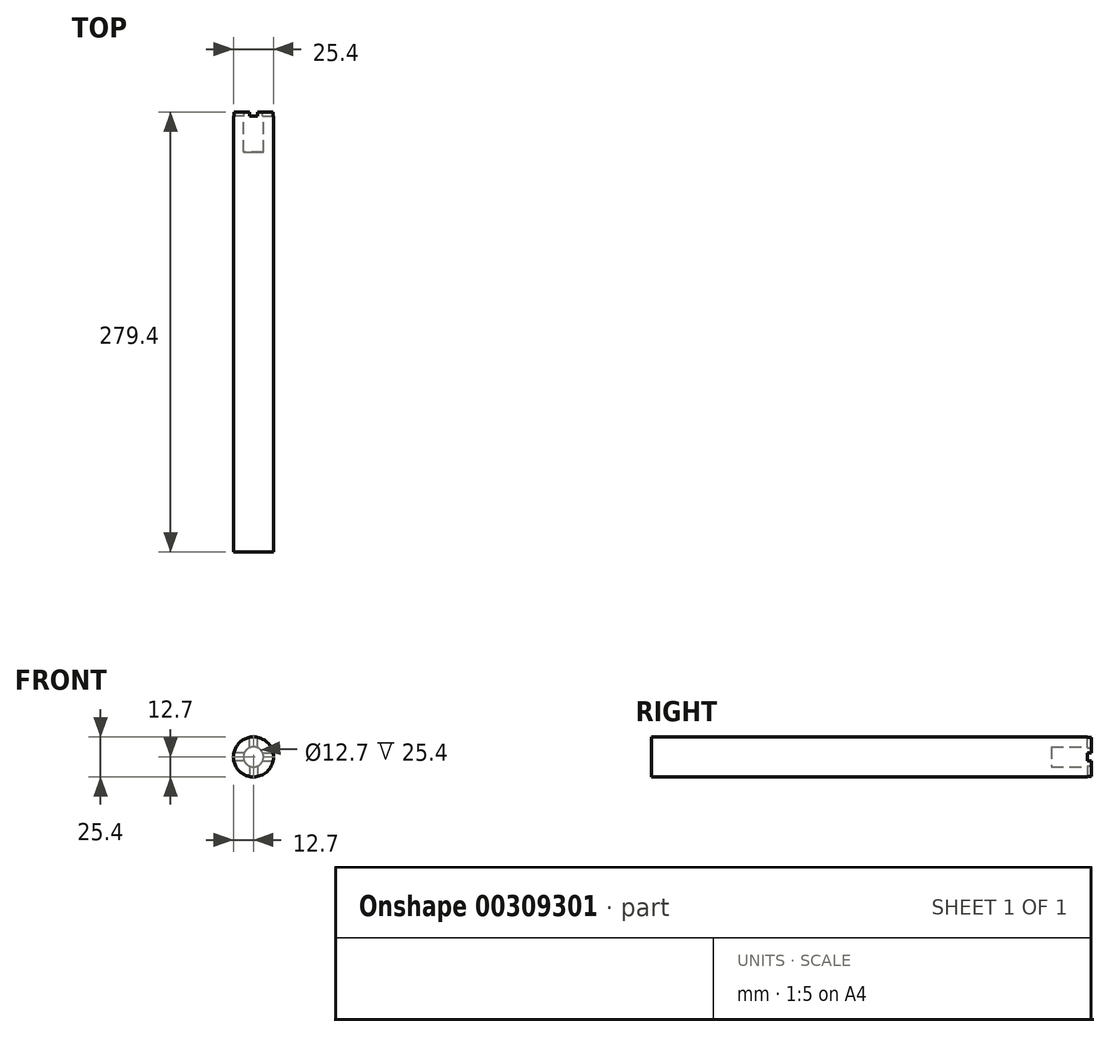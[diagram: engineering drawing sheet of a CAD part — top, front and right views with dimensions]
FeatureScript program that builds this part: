
annotation { "Feature Type Name" : "Feature", "Feature Type Description" : "" }
export const myFeature = defineFeature(function(context is Context, id is Id, definition is map)
    precondition{}
    {
        {
            var Q0;
            Q0=qCreatedBy(makeId("Front.planeOp"),FACE);
            var sketch = newSketch(context, id + "F0", { "sketchPlane" : qUnion([Q0])});
            skCircle(sketch, "E0", {"center": v(0, 0) * mm, "radius": 12.7 * mm});
            skSolve(sketch);
        }
        {
            var Q0;
            Q0 = qSketchRegion(id + "F0", true);
            extrude(context, id + "F1", {"entities" : qUnion([Q0]), "depth" : 279.4 * mm});
        }
        {
            var Q0;
            Q0=makeQuery(id+"F1.opExtrude","CAP_FACE",FACE,{"disambiguationData":[OSD([sQuery(id+"F0.wireOp",EDGE,"E0")])],"isStart":true});
            var sketch = newSketch(context, id + "F2", { "sketchPlane" : qUnion([Q0])});
            skCircle(sketch, "E1", {"center": v(0, 0) * mm, "radius": 6.35 * mm});
            skLineSegment(sketch, "E2", {"start": v(0, 31.25) * mm, "end": v(0, -36.33) * mm, "construction": true});
            skLineSegment(sketch, "E3", {"start": v(-5.82, -2.54) * mm, "end": v(-12.44, -2.54) * mm});
            skPoint(sketch, "E3.startSnap0", {"position": v(0, -2.54) * mm});
            skLineSegment(sketch, "E4", {"start": v(-5.82, 2.54) * mm, "end": v(-12.44, 2.54) * mm});
            skLineSegment(sketch, "E5", {"start": v(-2.54, 5.82) * mm, "end": v(-2.54, 12.44) * mm});
            skLineSegment(sketch, "E6", {"start": v(-2.54, -5.82) * mm, "end": v(-2.54, -12.44) * mm});
            skLineSegment(sketch, "E7.MirrorCS", {"start": v(2.54, 5.82) * mm, "end": v(2.54, 12.44) * mm});
            skLineSegment(sketch, "E8.MirrorCS", {"start": v(5.82, 2.54) * mm, "end": v(12.44, 2.54) * mm});
            skLineSegment(sketch, "E9.MirrorCS", {"start": v(5.82, -2.54) * mm, "end": v(12.44, -2.54) * mm});
            skLineSegment(sketch, "E10.MirrorCS", {"start": v(2.54, -5.82) * mm, "end": v(2.54, -12.44) * mm});
            skSolve(sketch);
        }
        {
            var Q0;
            {var subQ0=sQuery(id+"F2.wireOp",EDGE,"E1");var subQ4=makeQuery(id+"F2.imprint","INTERSECT",VERTEX,{"derivedFrom":[subQ0,sQuery(id+"F2.wireOp",EDGE,"E7.MirrorCS")]});Q0=makeQuery(id+"F2.imprint","IMPRINT",FACE,{"disambiguationData":[TD([[makeQuery(id+"F2.imprint","IMPRINT",EDGE,{"disambiguationData":[TD([[subQ4,1.0]])],"derivedFrom":subQ0}),1.0]])]});}
            extrude(context, id + "F3", {"entities" : qUnion([Q0]), "operationType" : NewBodyOperationType.REMOVE, "oppositeDirection" : true, "depth" : 25.4 * mm});
        }
        {
            var Q0;
            {var subQ0=sQuery(id+"F2.wireOp",EDGE,"E8.MirrorCS");Q0=makeQuery(id+"F2.imprint","IMPRINT",FACE,{"disambiguationData":[TD([[makeQuery(id+"F2.imprint","IMPRINT",EDGE,{"derivedFrom":subQ0}),-1.0]])]});}
            var Q1;
            {var subQ0=sQuery(id+"F2.wireOp",EDGE,"E5");Q1=makeQuery(id+"F2.imprint","IMPRINT",FACE,{"disambiguationData":[TD([[makeQuery(id+"F2.imprint","IMPRINT",EDGE,{"derivedFrom":subQ0}),-1.0]])]});}
            var Q2;
            {var subQ0=sQuery(id+"F2.wireOp",EDGE,"E6");Q2=makeQuery(id+"F2.imprint","IMPRINT",FACE,{"disambiguationData":[TD([[makeQuery(id+"F2.imprint","IMPRINT",EDGE,{"derivedFrom":subQ0}),1.0]])]});}
            var Q3;
            {var subQ0=sQuery(id+"F2.wireOp",EDGE,"E3");Q3=makeQuery(id+"F2.imprint","IMPRINT",FACE,{"disambiguationData":[TD([[makeQuery(id+"F2.imprint","IMPRINT",EDGE,{"derivedFrom":subQ0}),-1.0]])]});}
            extrude(context, id + "F4", {"entities" : qUnion([Q0, Q1, Q2, Q3]), "operationType" : NewBodyOperationType.REMOVE, "oppositeDirection" : true, "depth" : 2.54 * mm});
        }
    });
